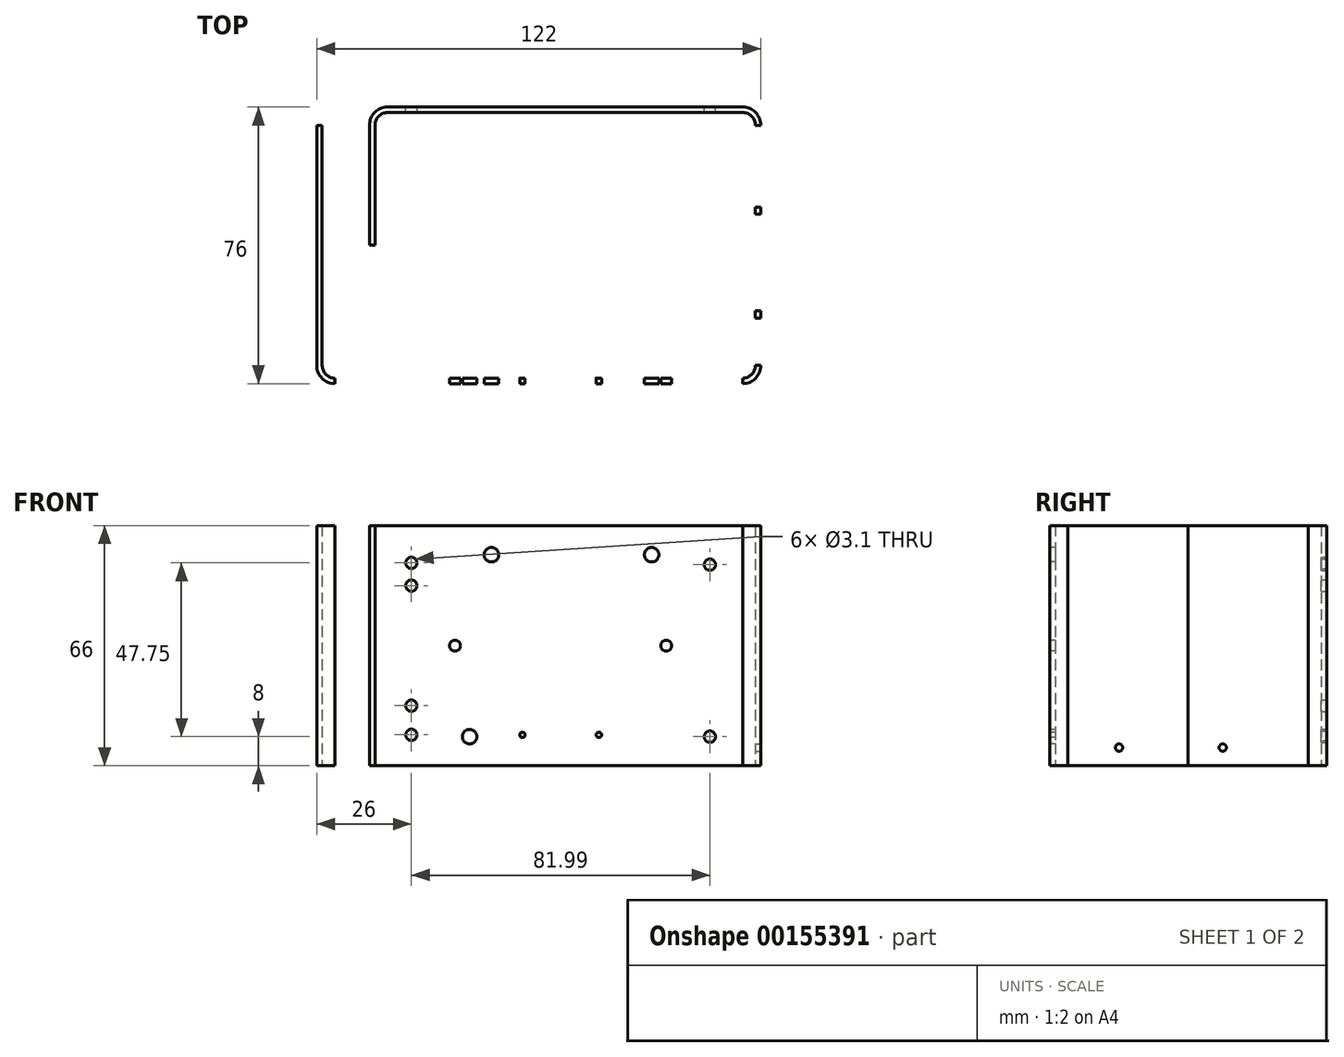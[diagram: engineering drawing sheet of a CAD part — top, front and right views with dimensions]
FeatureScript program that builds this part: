
annotation { "Feature Type Name" : "Feature", "Feature Type Description" : "" }
export const myFeature = defineFeature(function(context is Context, id is Id, definition is map)
    precondition{}
    {
        {
            var Q0;
            Q0=qCreatedBy(makeId("Top.planeOp"),FACE);
            var sketch = newSketch(context, id + "F0", { "sketchPlane" : qUnion([Q0])});
            skLineSegment(sketch, "E0", {"start": v(-66.75, 33) * mm, "end": v(-66.75, -33) * mm});
            skLineSegment(sketch, "E1", {"start": v(-63.25, -36.5) * mm, "end": v(48.75, -36.5) * mm});
            skLineSegment(sketch, "E2", {"start": v(52.25, -33) * mm, "end": v(52.25, 33) * mm});
            skLineSegment(sketch, "E3", {"start": v(48.75, 36.5) * mm, "end": v(-48.75, 36.5) * mm});
            skLineSegment(sketch, "E4", {"start": v(-52.25, 33) * mm, "end": v(-52.25, 0) * mm});
            skLineSegment(sketch, "E5.0", {"start": v(-53.75, 33) * mm, "end": v(-53.75, 0) * mm});
            skLineSegment(sketch, "E5.1", {"start": v(-68.25, 33) * mm, "end": v(-68.25, -33) * mm});
            skLineSegment(sketch, "E5.2", {"start": v(-63.25, -38) * mm, "end": v(48.75, -38) * mm});
            skLineSegment(sketch, "E5.3", {"start": v(53.75, -33) * mm, "end": v(53.75, 33) * mm});
            skLineSegment(sketch, "E5.4", {"start": v(48.75, 38) * mm, "end": v(-48.75, 38) * mm});
            skLineSegment(sketch, "E6", {"start": v(-52.25, 0) * mm, "end": v(-53.75, 0) * mm});
            skLineSegment(sketch, "E7", {"start": v(-66.75, 33) * mm, "end": v(-68.25, 33) * mm});
            skPoint(sketch, "E8.visualSharp", {"position": v(-66.75, -36.5) * mm});
            skArc(sketch, "E8.filletArc", {"start": v(-66.75, -33) * mm, "mid": v(-65.72, -35.47) * mm, "end": v(-63.25, -36.5) * mm});
            skPoint(sketch, "E9.visualSharp", {"position": v(52.25, -36.5) * mm});
            skArc(sketch, "E9.filletArc", {"start": v(48.75, -36.5) * mm, "mid": v(51.22, -35.47) * mm, "end": v(52.25, -33) * mm});
            skPoint(sketch, "E10.visualSharp", {"position": v(52.25, 36.5) * mm});
            skArc(sketch, "E10.filletArc", {"start": v(52.25, 33) * mm, "mid": v(51.22, 35.47) * mm, "end": v(48.75, 36.5) * mm});
            skPoint(sketch, "E11.visualSharp", {"position": v(-52.25, 36.5) * mm});
            skArc(sketch, "E11.filletArc", {"start": v(-48.75, 36.5) * mm, "mid": v(-51.22, 35.47) * mm, "end": v(-52.25, 33) * mm});
            skPoint(sketch, "E12.visualSharp", {"position": v(-68.25, -38) * mm});
            skArc(sketch, "E12.filletArc", {"start": v(-68.25, -33) * mm, "mid": v(-66.79, -36.54) * mm, "end": v(-63.25, -38) * mm});
            skPoint(sketch, "E13.visualSharp", {"position": v(53.75, -38) * mm});
            skArc(sketch, "E13.filletArc", {"start": v(48.75, -38) * mm, "mid": v(52.29, -36.54) * mm, "end": v(53.75, -33) * mm});
            skPoint(sketch, "E14.visualSharp", {"position": v(53.75, 38) * mm});
            skArc(sketch, "E14.filletArc", {"start": v(53.75, 33) * mm, "mid": v(52.29, 36.54) * mm, "end": v(48.75, 38) * mm});
            skPoint(sketch, "E15.visualSharp", {"position": v(-53.75, 38) * mm});
            skArc(sketch, "E15.filletArc", {"start": v(-48.75, 38) * mm, "mid": v(-52.29, 36.54) * mm, "end": v(-53.75, 33) * mm});
            skLineSegment(sketch, "E16", {"start": v(52.25, 0) * mm, "end": v(-12.48, 0) * mm, "construction": true});
            skLineSegment(sketch, "E17", {"start": v(0, 36.5) * mm, "end": v(0, -15.26) * mm, "construction": true});
            skSolve(sketch);
        }
        {
            var Q0;
            Q0=qSketchRegion(id+"F0",true);
            extrude(context, id + "F1", {"entities" : qUnion([Q0]), "depth" : 66 * mm});
        }
        {
            var Q0;
            Q0=makeQuery(id+"F1.opExtrude","SWEPT_FACE",FACE,{"disambiguationData":[OSD([sQuery(id+"F0.wireOp",EDGE,"E5.2")])]});
            var sketch = newSketch(context, id + "F2", { "sketchPlane" : qUnion([Q0])});
            skLineSegment(sketch, "E18.bottom", {"start": v(-23.25, 52) * mm, "end": v(20.75, 52) * mm});
            skLineSegment(sketch, "E18.top", {"start": v(-23.25, 14) * mm, "end": v(20.75, 14) * mm});
            skLineSegment(sketch, "E18.left", {"start": v(-26.25, 49) * mm, "end": v(-26.25, 17) * mm});
            skLineSegment(sketch, "E18.right", {"start": v(23.75, 49) * mm, "end": v(23.75, 17) * mm});
            skLineSegment(sketch, "E19", {"start": v(-63.25, 33) * mm, "end": v(43.75, 33) * mm, "construction": true});
            skLineSegment(sketch, "E20", {"start": v(23.75, 33) * mm, "end": v(-26.25, 33) * mm, "construction": true});
            skLineSegment(sketch, "E21", {"start": v(-1.25, 52) * mm, "end": v(-1.25, 14) * mm, "construction": true});
            skLineSegment(sketch, "E22", {"start": v(-7.25, 66) * mm, "end": v(-7.25, 0) * mm, "construction": true});
            skPoint(sketch, "E23.visualSharp", {"position": v(-26.25, 52) * mm});
            skArc(sketch, "E23.filletArc", {"start": v(-23.25, 52) * mm, "mid": v(-25.37, 51.12) * mm, "end": v(-26.25, 49) * mm});
            skPoint(sketch, "E24.visualSharp", {"position": v(23.75, 52) * mm});
            skArc(sketch, "E24.filletArc", {"start": v(23.75, 49) * mm, "mid": v(22.87, 51.12) * mm, "end": v(20.75, 52) * mm});
            skPoint(sketch, "E25.visualSharp", {"position": v(23.75, 14) * mm});
            skArc(sketch, "E25.filletArc", {"start": v(20.75, 14) * mm, "mid": v(22.87, 14.88) * mm, "end": v(23.75, 17) * mm});
            skPoint(sketch, "E26.visualSharp", {"position": v(-26.25, 14) * mm});
            skArc(sketch, "E26.filletArc", {"start": v(-26.25, 17) * mm, "mid": v(-25.37, 14.88) * mm, "end": v(-23.25, 14) * mm});
            skCircle(sketch, "E27", {"center": v(-30.25, 33) * mm, "radius": 1.5 * mm});
            skCircle(sketch, "E28.MirrorC", {"center": v(27.75, 33) * mm, "radius": 1.5 * mm});
            skCircle(sketch, "E29", {"center": v(-26.25, 58) * mm, "radius": 2 * mm});
            skCircle(sketch, "E30.MirrorC", {"center": v(23.75, 58) * mm, "radius": 2 * mm});
            skCircle(sketch, "E31.MirrorC", {"center": v(-26.25, 8) * mm, "radius": 2 * mm});
            skCircle(sketch, "E32.MirrorC", {"center": v(23.75, 8) * mm, "radius": 2 * mm});
            skLineSegment(sketch, "E33.bottom", {"start": v(-7.25, 7) * mm, "end": v(4.75, 7) * mm});
            skPoint(sketch, "E34.visualSharp", {"position": v(6.25, 10) * mm});
            skLineSegment(sketch, "E33.top", {"start": v(-7.25, 10) * mm, "end": v(4.75, 10) * mm});
            skArc(sketch, "E35.filletArc", {"start": v(-7.25, 10) * mm, "mid": v(-8.31, 9.56) * mm, "end": v(-8.75, 8.5) * mm});
            skLineSegment(sketch, "E33.left", {"start": v(-8.75, 8.5) * mm, "end": v(-8.75, 8.5) * mm});
            skLineSegment(sketch, "E33.right", {"start": v(6.25, 8.5) * mm, "end": v(6.25, 8.5) * mm});
            skArc(sketch, "E36.filletArc", {"start": v(-8.75, 8.5) * mm, "mid": v(-8.31, 7.44) * mm, "end": v(-7.25, 7) * mm});
            skArc(sketch, "E37.filletArc", {"start": v(4.75, 7) * mm, "mid": v(5.81, 7.44) * mm, "end": v(6.25, 8.5) * mm});
            skArc(sketch, "E34.filletArc", {"start": v(6.25, 8.5) * mm, "mid": v(5.81, 9.56) * mm, "end": v(4.75, 10) * mm});
            skCircle(sketch, "E38", {"center": v(-11.75, 8.5) * mm, "radius": 0.75 * mm});
            skPoint(sketch, "E39", {"position": v(-1.25, 10) * mm});
            skLineSegment(sketch, "E40", {"start": v(-11.75, 8.5) * mm, "end": v(6.89, 8.5) * mm, "construction": true});
            skPoint(sketch, "E35.visualSharp", {"position": v(-8.75, 10) * mm});
            skPoint(sketch, "E36.visualSharp", {"position": v(-8.75, 7) * mm});
            skPoint(sketch, "E37.visualSharp", {"position": v(6.25, 7) * mm});
            skLineSegment(sketch, "E41", {"start": v(-1.25, 10) * mm, "end": v(-1.25, 7) * mm, "construction": true});
            skCircle(sketch, "E42.MirrorC", {"center": v(9.25, 8.5) * mm, "radius": 0.75 * mm});
            skLineSegment(sketch, "E43", {"start": v(-26.25, 8) * mm, "end": v(-26.25, 58) * mm, "construction": true});
            skLineSegment(sketch, "E44", {"start": v(23.75, 58) * mm, "end": v(23.75, 8) * mm, "construction": true});
            skLineSegment(sketch, "E45", {"start": v(-26.25, 8) * mm, "end": v(23.75, 8) * mm, "construction": true});
            skLineSegment(sketch, "E46", {"start": v(23.75, 58) * mm, "end": v(-26.25, 58) * mm, "construction": true});
            skCircle(sketch, "E47", {"center": v(-20.25, 8) * mm, "radius": 2 * mm});
            skCircle(sketch, "E48.MirrorC", {"center": v(-20.25, 58) * mm, "radius": 2 * mm});
            skCircle(sketch, "E49.MirrorC", {"center": v(17.75, 58) * mm, "radius": 2 * mm});
            skCircle(sketch, "E50", {"center": v(14.75, 8) * mm, "radius": 2 * mm});
            skPoint(sketch, "E51", {"position": v(-63.25, 33) * mm});
            skSolve(sketch);
        }
        {
            var Q0;
            Q0=makeQuery(id+"F2.imprint","IMPRINT",FACE,{"disambiguationData":[TD([[makeQuery(id+"F2.imprint","IMPRINT",EDGE,{"derivedFrom":sQuery(id+"F2.wireOp",EDGE,"E18.bottom")}),-1.0]])]});
            var Q1;
            Q1=makeQuery(id+"F2.imprint","IMPRINT",FACE,{"disambiguationData":[TD([[makeQuery(id+"F2.imprint","IMPRINT",EDGE,{"derivedFrom":sQuery(id+"F2.wireOp",EDGE,"5223969e-9384-4705-a09f-08a9d0864926")}),1.0]])]});
            var Q2;
            Q2=makeQuery(id+"F2.imprint","IMPRINT",FACE,{"disambiguationData":[TD([[makeQuery(id+"F2.imprint","IMPRINT",EDGE,{"derivedFrom":sQuery(id+"F2.wireOp",EDGE,"b6238159-0034-45e9-8c88-9dabcd8353630.MirrorC")}),-1.0]])]});
            var Q3;
            Q3=makeQuery(id+"F2.imprint","IMPRINT",FACE,{"disambiguationData":[TD([[makeQuery(id+"F2.imprint","IMPRINT",EDGE,{"derivedFrom":sQuery(id+"F2.wireOp",EDGE,"E29")}),1.0]])]});
            var Q4;
            Q4=makeQuery(id+"F2.imprint","IMPRINT",FACE,{"disambiguationData":[TD([[makeQuery(id+"F2.imprint","IMPRINT",EDGE,{"derivedFrom":sQuery(id+"F2.wireOp",EDGE,"E30.MirrorC")}),-1.0]])]});
            var Q5;
            Q5=makeQuery(id+"F2.imprint","IMPRINT",FACE,{"disambiguationData":[TD([[makeQuery(id+"F2.imprint","IMPRINT",EDGE,{"derivedFrom":sQuery(id+"F2.wireOp",EDGE,"E32.MirrorC")}),1.0]])]});
            var Q6;
            Q6=makeQuery(id+"F2.imprint","IMPRINT",FACE,{"disambiguationData":[TD([[makeQuery(id+"F2.imprint","IMPRINT",EDGE,{"derivedFrom":sQuery(id+"F2.wireOp",EDGE,"E31.MirrorC")}),-1.0]])]});
            var Q7;
            Q7=makeQuery(id+"F2.imprint","IMPRINT",FACE,{"disambiguationData":[TD([[makeQuery(id+"F2.imprint","IMPRINT",EDGE,{"derivedFrom":sQuery(id+"F2.wireOp",EDGE,"E33.bottom")}),1.0]])]});
            var Q8;
            Q8=makeQuery(id+"F2.imprint","IMPRINT",FACE,{"disambiguationData":[TD([[makeQuery(id+"F2.imprint","IMPRINT",EDGE,{"derivedFrom":sQuery(id+"F2.wireOp",EDGE,"E47")}),1.0]])]});
            var Q9;
            Q9=makeQuery(id+"F2.imprint","IMPRINT",FACE,{"disambiguationData":[TD([[makeQuery(id+"F2.imprint","IMPRINT",EDGE,{"derivedFrom":sQuery(id+"F2.wireOp",EDGE,"E48.MirrorC")}),-1.0]])]});
            var Q10;
            Q10=makeQuery(id+"F2.imprint","IMPRINT",FACE,{"disambiguationData":[TD([[makeQuery(id+"F2.imprint","IMPRINT",EDGE,{"derivedFrom":sQuery(id+"F2.wireOp",EDGE,"E49.MirrorC")}),1.0]])]});
            var Q11;
            Q11=makeQuery(id+"F2.imprint","IMPRINT",FACE,{"disambiguationData":[TD([[makeQuery(id+"F2.imprint","IMPRINT",EDGE,{"derivedFrom":sQuery(id+"F2.wireOp",EDGE,"E50")}),1.0]])]});
            extrude(context, id + "F3", {"entities" : qUnion([Q0, Q1, Q2, Q3, Q4, Q5, Q6, Q7, Q8, Q9, Q10, Q11]), "operationType" : NewBodyOperationType.REMOVE, "oppositeDirection" : true, "depth" : 25 * mm});
        }
        {
            var Q0;
            Q0=makeQuery(id+"F1.opExtrude","SWEPT_FACE",FACE,{"disambiguationData":[OSD([sQuery(id+"F0.wireOp",EDGE,"E5.4")])]});
            var sketch = newSketch(context, id + "F4", { "sketchPlane" : qUnion([Q0])});
            skCircle(sketch, "E52", {"center": v(-39.74, 55.25) * mm, "radius": 1.55 * mm});
            skLineSegment(sketch, "E53", {"start": v(-39.74, 55.25) * mm, "end": v(-39.74, 8) * mm, "construction": true});
            skLineSegment(sketch, "E54", {"start": v(42.25, 8.5) * mm, "end": v(42.25, 55.75) * mm, "construction": true});
            skCircle(sketch, "E55", {"center": v(-39.74, 8) * mm, "radius": 1.55 * mm});
            skCircle(sketch, "E56", {"center": v(42.25, 8.5) * mm, "radius": 1.55 * mm});
            skCircle(sketch, "E57", {"center": v(42.25, 55.75) * mm, "radius": 1.55 * mm});
            skPoint(sketch, "E58.endSnap0", {"position": v(0, 0) * mm});
            skCircle(sketch, "E59", {"center": v(42.25, 49.5) * mm, "radius": 1.55 * mm});
            skCircle(sketch, "E60", {"center": v(42.25, 16.5) * mm, "radius": 1.55 * mm});
            skLineSegment(sketch, "E61", {"start": v(33.75, 66) * mm, "end": v(33.75, 0) * mm, "construction": true});
            skLineSegment(sketch, "E62", {"start": v(33.75, 33) * mm, "end": v(24.95, 33) * mm, "construction": true});
            skLineSegment(sketch, "E63", {"start": v(29.35, 33) * mm, "end": v(29.35, 66) * mm, "construction": true});
            skLineSegment(sketch, "E64", {"start": v(29.35, 33) * mm, "end": v(29.35, 0) * mm, "construction": true});
            skLineSegment(sketch, "E65", {"start": v(29.35, 16.5) * mm, "end": v(44.25, 16.5) * mm, "construction": true});
            skLineSegment(sketch, "E66", {"start": v(29.35, 49.5) * mm, "end": v(45.75, 49.5) * mm, "construction": true});
            skSolve(sketch);
        }
        {
            var Q0;
            Q0=makeQuery(id+"F4.imprint","IMPRINT",FACE,{"disambiguationData":[TD([[makeQuery(id+"F4.imprint","IMPRINT",EDGE,{"derivedFrom":sQuery(id+"F4.wireOp",EDGE,"E52")}),1.0]])]});
            var Q1;
            Q1=makeQuery(id+"F4.imprint","IMPRINT",FACE,{"disambiguationData":[TD([[makeQuery(id+"F4.imprint","IMPRINT",EDGE,{"derivedFrom":sQuery(id+"F4.wireOp",EDGE,"E55")}),1.0]])]});
            var Q2;
            Q2=makeQuery(id+"F4.imprint","IMPRINT",FACE,{"disambiguationData":[TD([[makeQuery(id+"F4.imprint","IMPRINT",EDGE,{"derivedFrom":sQuery(id+"F4.wireOp",EDGE,"E56")}),1.0]])]});
            var Q3;
            Q3=makeQuery(id+"F4.imprint","IMPRINT",FACE,{"disambiguationData":[TD([[makeQuery(id+"F4.imprint","IMPRINT",EDGE,{"derivedFrom":sQuery(id+"F4.wireOp",EDGE,"E57")}),1.0]])]});
            var Q4;
            Q4=makeQuery(id+"F4.imprint","IMPRINT",FACE,{"disambiguationData":[TD([[makeQuery(id+"F4.imprint","IMPRINT",EDGE,{"derivedFrom":sQuery(id+"F4.wireOp",EDGE,"E60")}),1.0]])]});
            var Q5;
            Q5=makeQuery(id+"F4.imprint","IMPRINT",FACE,{"disambiguationData":[TD([[makeQuery(id+"F4.imprint","IMPRINT",EDGE,{"derivedFrom":sQuery(id+"F4.wireOp",EDGE,"E59")}),1.0]])]});
            extrude(context, id + "F5", {"entities" : qUnion([Q0, Q1, Q2, Q3, Q4, Q5]), "operationType" : NewBodyOperationType.REMOVE, "oppositeDirection" : true, "depth" : 25 * mm});
        }
        {
            var Q0;
            Q0=makeQuery(id+"F1.opExtrude","SWEPT_FACE",FACE,{"disambiguationData":[OSD([sQuery(id+"F0.wireOp",EDGE,"E5.3")])]});
            var sketch = newSketch(context, id + "F6", { "sketchPlane" : qUnion([Q0])});
            skLineSegment(sketch, "E67.bottom", {"start": v(-21, 58) * mm, "end": v(-17, 58) * mm});
            skLineSegment(sketch, "E67.top", {"start": v(-21, 8) * mm, "end": v(-17, 8) * mm});
            skLineSegment(sketch, "E67.left", {"start": v(-24, 55) * mm, "end": v(-24, 11) * mm});
            skLineSegment(sketch, "E67.right", {"start": v(-14, 55) * mm, "end": v(-14, 11) * mm});
            skLineSegment(sketch, "E68.bottom", {"start": v(-5, 58) * mm, "end": v(24, 58) * mm});
            skLineSegment(sketch, "E68.top", {"start": v(-5, 8) * mm, "end": v(24, 8) * mm});
            skLineSegment(sketch, "E68.left", {"start": v(-8, 55) * mm, "end": v(-8, 11) * mm});
            skLineSegment(sketch, "E68.right", {"start": v(27, 55) * mm, "end": v(27, 11) * mm});
            skLineSegment(sketch, "E69", {"start": v(-14, 58) * mm, "end": v(-8, 58) * mm, "construction": true});
            skLineSegment(sketch, "E70", {"start": v(-14, 8) * mm, "end": v(-8, 8) * mm, "construction": true});
            skPoint(sketch, "E71.visualSharp", {"position": v(-24, 58) * mm});
            skArc(sketch, "E71.filletArc", {"start": v(-21, 58) * mm, "mid": v(-23.12, 57.12) * mm, "end": v(-24, 55) * mm});
            skPoint(sketch, "E72.visualSharp", {"position": v(-14, 58) * mm});
            skArc(sketch, "E72.filletArc", {"start": v(-14, 55) * mm, "mid": v(-14.88, 57.12) * mm, "end": v(-17, 58) * mm});
            skPoint(sketch, "E73.visualSharp", {"position": v(-24, 8) * mm});
            skArc(sketch, "E73.filletArc", {"start": v(-24, 11) * mm, "mid": v(-23.12, 8.88) * mm, "end": v(-21, 8) * mm});
            skPoint(sketch, "E74.visualSharp", {"position": v(-14, 8) * mm});
            skArc(sketch, "E74.filletArc", {"start": v(-17, 8) * mm, "mid": v(-14.88, 8.88) * mm, "end": v(-14, 11) * mm});
            skPoint(sketch, "E75.visualSharp", {"position": v(-8, 8) * mm});
            skArc(sketch, "E75.filletArc", {"start": v(-8, 11) * mm, "mid": v(-7.12, 8.88) * mm, "end": v(-5, 8) * mm});
            skPoint(sketch, "E76.visualSharp", {"position": v(27, 8) * mm});
            skArc(sketch, "E76.filletArc", {"start": v(24, 8) * mm, "mid": v(26.12, 8.88) * mm, "end": v(27, 11) * mm});
            skPoint(sketch, "E77.visualSharp", {"position": v(27, 58) * mm});
            skArc(sketch, "E77.filletArc", {"start": v(27, 55) * mm, "mid": v(26.12, 57.12) * mm, "end": v(24, 58) * mm});
            skPoint(sketch, "E78.visualSharp", {"position": v(-8, 58) * mm});
            skArc(sketch, "E78.filletArc", {"start": v(-5, 58) * mm, "mid": v(-7.12, 57.12) * mm, "end": v(-8, 55) * mm});
            skCircle(sketch, "E79", {"center": v(-19, 61) * mm, "radius": 1 * mm});
            skLineSegment(sketch, "E80", {"start": v(-24, 33) * mm, "end": v(27, 33) * mm, "construction": true});
            skLineSegment(sketch, "E81", {"start": v(-19, 58) * mm, "end": v(-19, 8) * mm, "construction": true});
            skPoint(sketch, "E81.endSnap0", {"position": v(-19, 8) * mm});
            skLineSegment(sketch, "E82", {"start": v(9.5, 8) * mm, "end": v(9.5, 58) * mm, "construction": true});
            skCircle(sketch, "E83", {"center": v(9.5, 61) * mm, "radius": 1 * mm});
            skCircle(sketch, "E84.MirrorC", {"center": v(-19, 5) * mm, "radius": 1 * mm});
            skCircle(sketch, "E85.MirrorC", {"center": v(9.5, 5) * mm, "radius": 1 * mm});
            skSolve(sketch);
        }
        {
            var Q0;
            Q0=makeQuery(id+"F6.imprint","IMPRINT",FACE,{"disambiguationData":[TD([[makeQuery(id+"F6.imprint","IMPRINT",EDGE,{"derivedFrom":sQuery(id+"F6.wireOp",EDGE,"E67.bottom")}),-1.0]])]});
            var Q1;
            Q1=makeQuery(id+"F6.imprint","IMPRINT",FACE,{"disambiguationData":[TD([[makeQuery(id+"F6.imprint","IMPRINT",EDGE,{"derivedFrom":sQuery(id+"F6.wireOp",EDGE,"E68.bottom")}),-1.0]])]});
            var Q2;
            Q2=makeQuery(id+"F6.imprint","IMPRINT",FACE,{"disambiguationData":[TD([[makeQuery(id+"F6.imprint","IMPRINT",EDGE,{"derivedFrom":sQuery(id+"F6.wireOp",EDGE,"E67.bottom")}),-1.0]])]});
            var Q3;
            Q3=makeQuery(id+"F6.imprint","IMPRINT",FACE,{"disambiguationData":[TD([[makeQuery(id+"F6.imprint","IMPRINT",EDGE,{"derivedFrom":sQuery(id+"F6.wireOp",EDGE,"E68.bottom")}),-1.0]])]});
            var Q4;
            Q4=makeQuery(id+"F6.imprint","IMPRINT",FACE,{"disambiguationData":[TD([[makeQuery(id+"F6.imprint","IMPRINT",EDGE,{"derivedFrom":sQuery(id+"F6.wireOp",EDGE,"E79")}),1.0]])]});
            var Q5;
            Q5=makeQuery(id+"F6.imprint","IMPRINT",FACE,{"disambiguationData":[TD([[makeQuery(id+"F6.imprint","IMPRINT",EDGE,{"derivedFrom":sQuery(id+"F6.wireOp",EDGE,"E83")}),1.0]])]});
            var Q6;
            Q6=makeQuery(id+"F6.imprint","IMPRINT",FACE,{"disambiguationData":[TD([[makeQuery(id+"F6.imprint","IMPRINT",EDGE,{"derivedFrom":sQuery(id+"F6.wireOp",EDGE,"E85.MirrorC")}),-1.0]])]});
            var Q7;
            Q7=makeQuery(id+"F6.imprint","IMPRINT",FACE,{"disambiguationData":[TD([[makeQuery(id+"F6.imprint","IMPRINT",EDGE,{"derivedFrom":sQuery(id+"F6.wireOp",EDGE,"E84.MirrorC")}),-1.0]])]});
            extrude(context, id + "F7", {"entities" : qUnion([Q0, Q1, Q2, Q3, Q4, Q5, Q6, Q7]), "operationType" : NewBodyOperationType.REMOVE, "oppositeDirection" : true, "depth" : 25 * mm});
        }
    });
